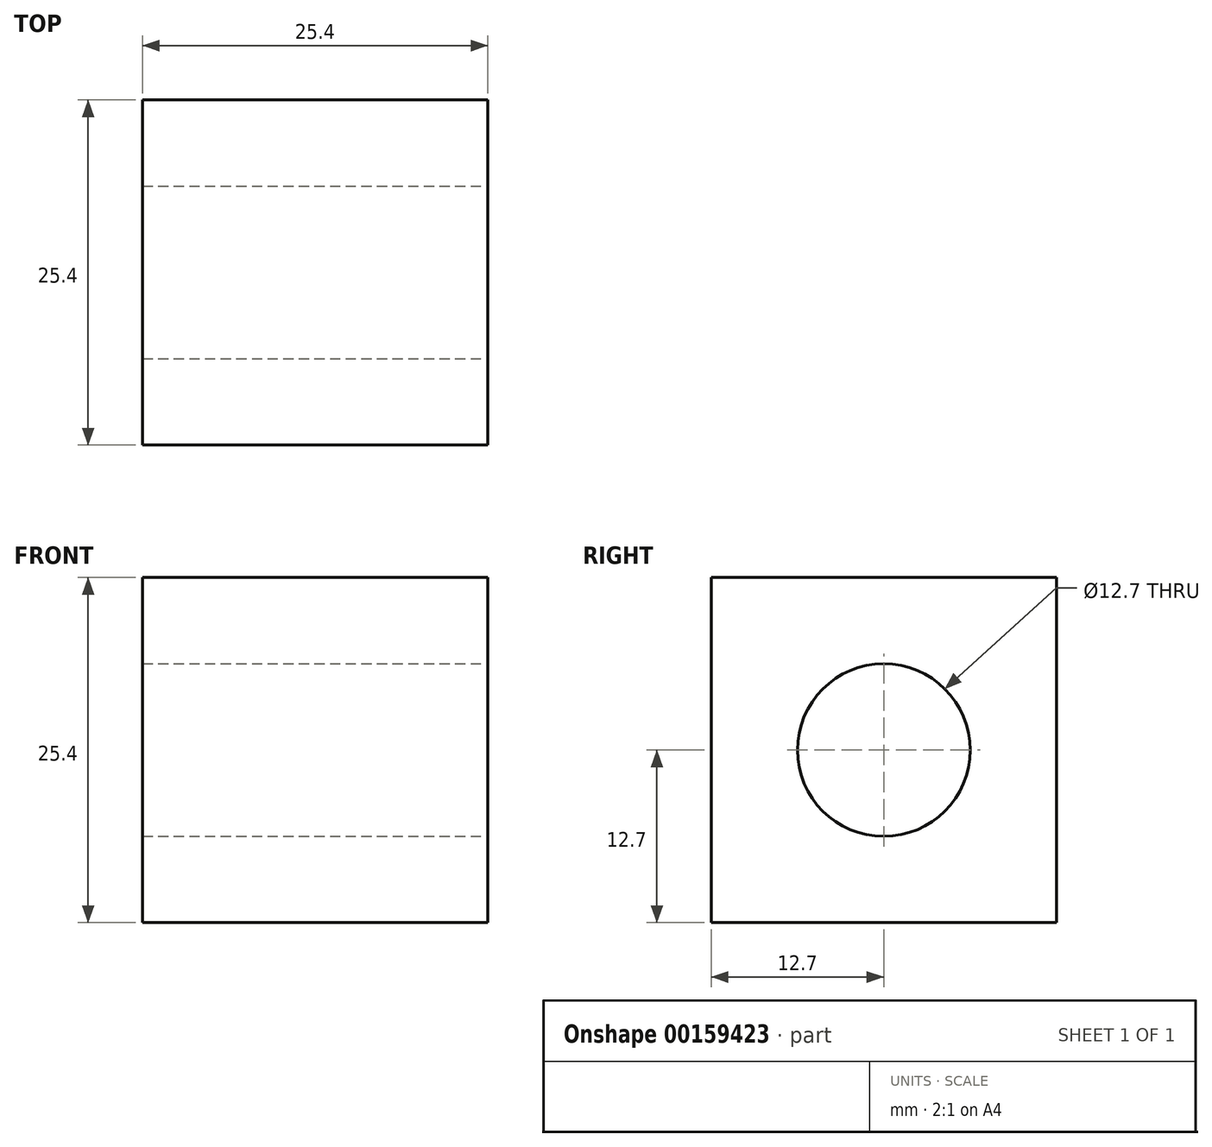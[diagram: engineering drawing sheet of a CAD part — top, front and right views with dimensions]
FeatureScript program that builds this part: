
annotation { "Feature Type Name" : "Feature", "Feature Type Description" : "" }
export const myFeature = defineFeature(function(context is Context, id is Id, definition is map)
    precondition{}
    {
        {
            var Q0;
            Q0=qCreatedBy(makeId("Top.planeOp"),FACE);
            var sketch = newSketch(context, id + "F0", { "sketchPlane" : qUnion([Q0])});
            skLineSegment(sketch, "E0.bottom", {"start": v(0, 0) * mm, "end": v(25.4, 0) * mm});
            skLineSegment(sketch, "E0.top", {"start": v(0, 25.4) * mm, "end": v(25.4, 25.4) * mm});
            skLineSegment(sketch, "E0.left", {"start": v(0, 0) * mm, "end": v(0, 25.4) * mm});
            skLineSegment(sketch, "E0.right", {"start": v(25.4, 0) * mm, "end": v(25.4, 25.4) * mm});
            skSolve(sketch);
        }
        {
            var Q0;
            Q0=makeQuery(id+"F0.imprint","IMPRINT",FACE,{"disambiguationData":[TD([[makeQuery(id+"F0.imprint","IMPRINT",EDGE,{"derivedFrom":sQuery(id+"F0.wireOp",EDGE,"E0.bottom")}),1.0]])]});
            extrude(context, id + "F1", {"entities" : qUnion([Q0]), "depth" : 25.4 * mm});
        }
        {
            var Q0;
            Q0=makeQuery(id+"F1.opExtrude","SWEPT_FACE",FACE,{"disambiguationData":[OSD([sQuery(id+"F0.wireOp",EDGE,"E0.right")])]});
            var sketch = newSketch(context, id + "F2", { "sketchPlane" : qUnion([Q0])});
            skLineSegment(sketch, "E1", {"start": v(0, 25.4) * mm, "end": v(25.4, 0) * mm, "construction": true});
            skCircle(sketch, "E2", {"center": v(12.7, 12.7) * mm, "radius": 6.35 * mm});
            skSolve(sketch);
        }
        {
            var Q0;
            Q0=makeQuery(id+"F2.imprint","IMPRINT",FACE,{"disambiguationData":[TD([[makeQuery(id+"F2.imprint","IMPRINT",EDGE,{"derivedFrom":sQuery(id+"F2.wireOp",EDGE,"E2")}),1.0]])]});
            extrude(context, id + "F3", {"entities" : qUnion([Q0]), "operationType" : NewBodyOperationType.REMOVE, "oppositeDirection" : true, "depth" : 25.4 * mm});
        }
    });
